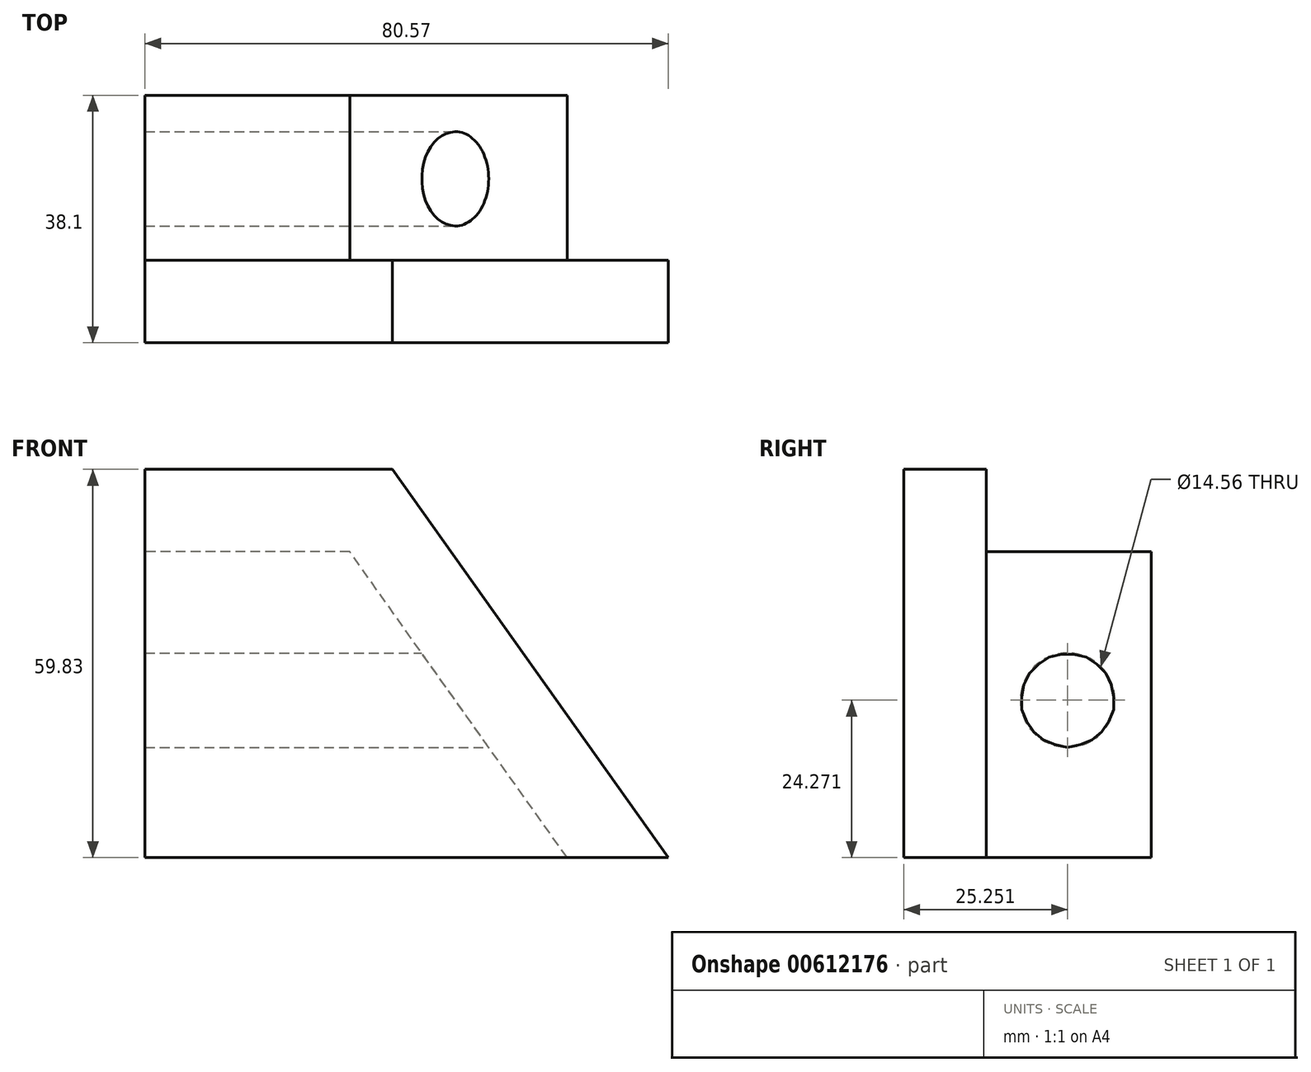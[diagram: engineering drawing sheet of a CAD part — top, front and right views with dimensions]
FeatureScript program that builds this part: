
annotation { "Feature Type Name" : "Feature", "Feature Type Description" : "" }
export const myFeature = defineFeature(function(context is Context, id is Id, definition is map)
    precondition{}
    {
        {
            var Q0;
            Q0=qCreatedBy(makeId("Front.planeOp"),FACE);
            var sketch = newSketch(context, id + "F0", { "sketchPlane" : qUnion([Q0])});
            skLineSegment(sketch, "E0", {"start": v(-27.27, -40.32) * mm, "end": v(53.3, -40.32) * mm});
            skLineSegment(sketch, "E1", {"start": v(53.3, -40.32) * mm, "end": v(10.83, 19.5) * mm});
            skLineSegment(sketch, "E2", {"start": v(10.83, 19.5) * mm, "end": v(-27.27, 19.5) * mm});
            skLineSegment(sketch, "E3", {"start": v(-27.27, 19.5) * mm, "end": v(-27.27, -40.32) * mm});
            skLineSegment(sketch, "E4.0", {"start": v(4.27, 6.8) * mm, "end": v(-27.27, 6.8) * mm});
            skLineSegment(sketch, "E4.1", {"start": v(37.72, -40.32) * mm, "end": v(4.27, 6.8) * mm});
            skSolve(sketch);
        }
        {
            var Q0;
            {var subQ4=sQuery(id+"F0.wireOp",EDGE,"E4.0");Q0=makeQuery(id+"F0.imprint","IMPRINT",FACE,{"disambiguationData":[TD([[makeQuery(id+"F0.imprint","IMPRINT",EDGE,{"derivedFrom":subQ4}),1.0]])]});}
            extrude(context, id + "F1", {"entities" : qUnion([Q0]), "oppositeDirection" : true, "depth" : 25.4 * mm, "offsetDistance" : 25.4 * mm});
        }
        {
            var Q0;
            Q0 = qSketchRegion(id + "F0", true);
            extrude(context, id + "F2", {"entities" : qUnion([Q0]), "operationType" : NewBodyOperationType.ADD, "depth" : 12.7 * mm, "offsetDistance" : 25.4 * mm});
        }
        {
            var Q0;
            Q0=qCreatedBy(makeId("Right.planeOp"),FACE);
            var sketch = newSketch(context, id + "F3", { "sketchPlane" : qUnion([Q0])});
            skCircle(sketch, "E5", {"center": v(12.55, -16.05) * mm, "radius": 7.28 * mm});
            skSolve(sketch);
        }
        {
            var Q0;
            Q0 = qSketchRegion(id + "F3", true);
            extrude(context, id + "F4", {"entities" : qUnion([Q0]), "operationType" : NewBodyOperationType.REMOVE, "oppositeDirection" : true, "depth" : 127 * mm, "offsetDistance" : 25.4 * mm, "symmetric" : true});
        }
    });
